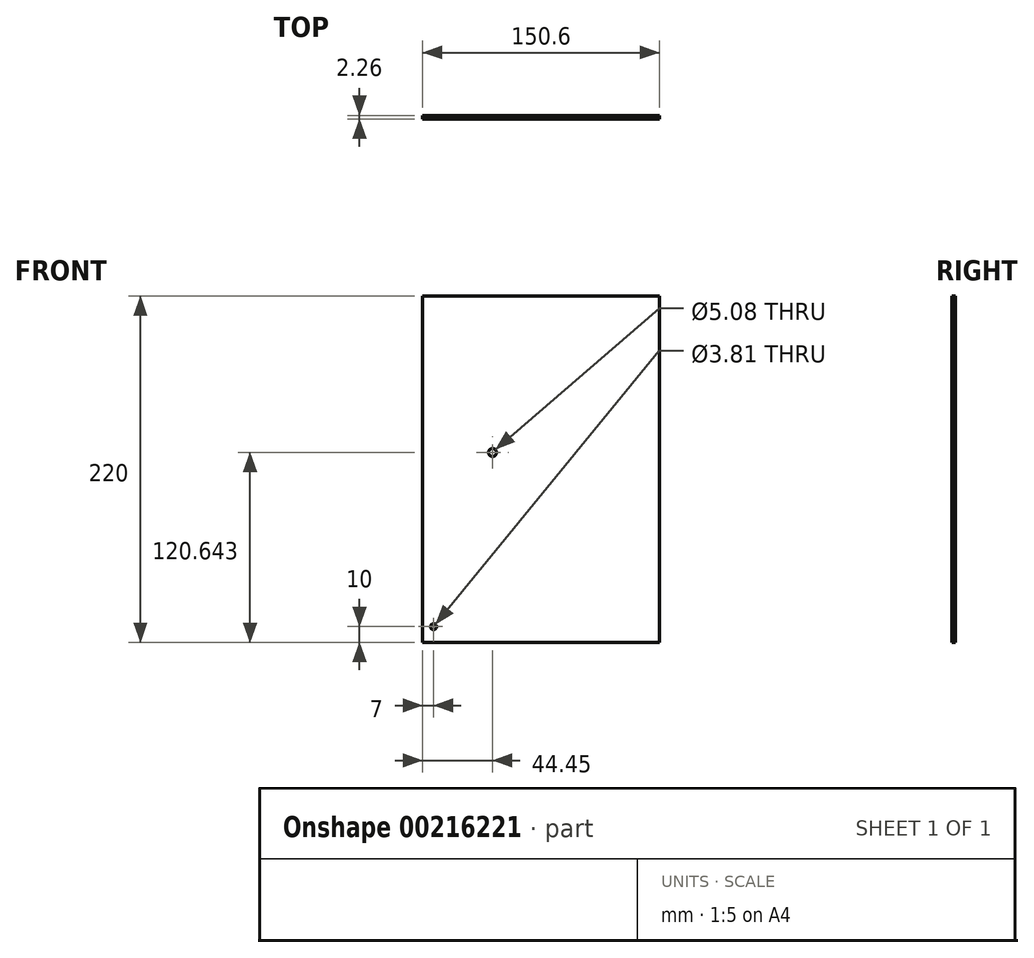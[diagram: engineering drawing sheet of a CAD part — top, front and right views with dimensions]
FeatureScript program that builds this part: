
annotation { "Feature Type Name" : "Feature", "Feature Type Description" : "" }
export const myFeature = defineFeature(function(context is Context, id is Id, definition is map)
    precondition{}
    {
        {
            var Q0;
            Q0=qCreatedBy(makeId("Front.planeOp"),FACE);
            var sketch = newSketch(context, id + "F0", { "sketchPlane" : qUnion([Q0])});
            skLineSegment(sketch, "E0.bottom", {"start": v(75.3, 110) * mm, "end": v(-75.3, 110) * mm});
            skLineSegment(sketch, "E0.top", {"start": v(75.3, -110) * mm, "end": v(-75.3, -110) * mm});
            skLineSegment(sketch, "E0.left", {"start": v(75.3, 110) * mm, "end": v(75.3, -110) * mm});
            skLineSegment(sketch, "E0.right", {"start": v(-75.3, 110) * mm, "end": v(-75.3, -110) * mm});
            skPoint(sketch, "E0.middle", {"position": v(0, 0) * mm});
            skLineSegment(sketch, "E1", {"start": v(-75.3, 0) * mm, "end": v(-30.85, 0) * mm, "construction": true});
            skPoint(sketch, "E1.endSnap0", {"position": v(-75.3, 0) * mm});
            skLineSegment(sketch, "E2", {"start": v(-30.85, 10.64) * mm, "end": v(-30.85, 0) * mm, "construction": true});
            skCircle(sketch, "E3", {"center": v(-30.85, 10.64) * mm, "radius": 2.54 * mm});
            skLineSegment(sketch, "E4", {"start": v(-75.3, -110) * mm, "end": v(-75.3, -100) * mm});
            skLineSegment(sketch, "E5", {"start": v(-75.3, -100) * mm, "end": v(-68.3, -100) * mm});
            skCircle(sketch, "E6", {"center": v(-68.3, -100) * mm, "radius": 1.9 * mm});
            skSolve(sketch);
        }
        {
            var Q0;
            Q0=makeQuery(id+"F0.imprint","IMPRINT",FACE,{"disambiguationData":[TD([[makeQuery(id+"F0.imprint","IMPRINT",EDGE,{"derivedFrom":sQuery(id+"F0.wireOp",EDGE,"E0.bottom")}),1.0]])]});
            extrude(context, id + "F1", {"entities" : qUnion([Q0]), "endBound" : BoundingType.SYMMETRIC, "depth" : 2.26 * mm});
        }
    });
